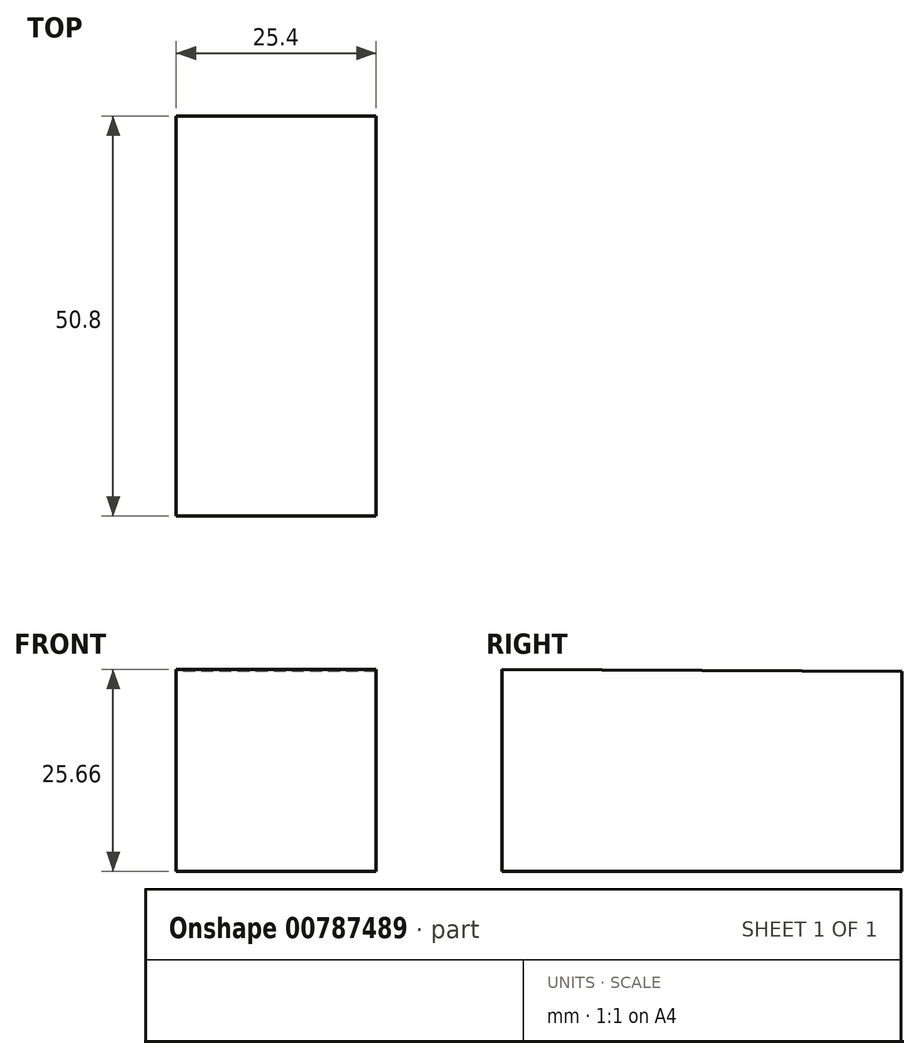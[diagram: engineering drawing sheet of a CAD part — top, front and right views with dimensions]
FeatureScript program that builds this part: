
annotation { "Feature Type Name" : "Feature", "Feature Type Description" : "" }
export const myFeature = defineFeature(function(context is Context, id is Id, definition is map)
    precondition{}
    {
        {
            var Q0;
            Q0=qCreatedBy(makeId("Right.planeOp"),FACE);
            var sketch = newSketch(context, id + "F0", { "sketchPlane" : qUnion([Q0])});
            skLineSegment(sketch, "E0", {"start": v(0, 25.4) * mm, "end": v(0, 0) * mm});
            skLineSegment(sketch, "E1", {"start": v(0, 0) * mm, "end": v(-50.8, 0) * mm});
            skLineSegment(sketch, "E2", {"start": v(-50.8, 0) * mm, "end": v(-50.8, 25.66) * mm});
            skLineSegment(sketch, "E3", {"start": v(-50.8, 25.66) * mm, "end": v(0, 25.4) * mm});
            skSolve(sketch);
        }
        {
            var Q0;
            Q0 = qSketchRegion(id + "F0", true);
            extrude(context, id + "F1", {"entities" : qUnion([Q0]), "depth" : 25.4 * mm, "offsetDistance" : 25.4 * mm});
        }
    });
